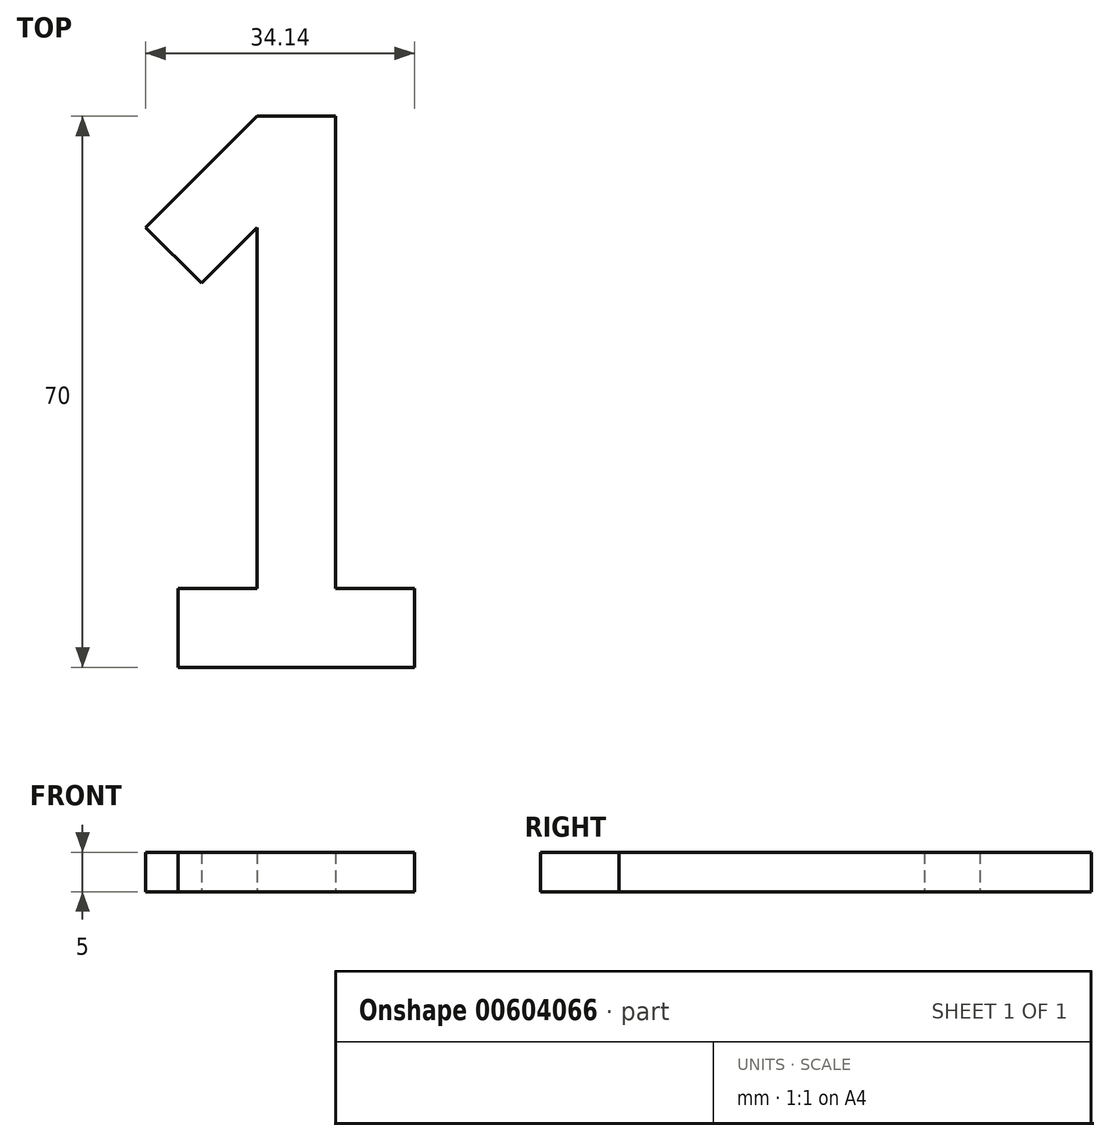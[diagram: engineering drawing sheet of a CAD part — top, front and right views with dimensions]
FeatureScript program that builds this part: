
annotation { "Feature Type Name" : "Feature", "Feature Type Description" : "" }
export const myFeature = defineFeature(function(context is Context, id is Id, definition is map)
    precondition{}
    {
        {
            var Q0;
            Q0=qCreatedBy(makeId("Top.planeOp"),FACE);
            var sketch = newSketch(context, id + "F0", { "sketchPlane" : qUnion([Q0])});
            skLineSegment(sketch, "E0.bottom", {"start": v(-3.56, 0) * mm, "end": v(6.44, 0) * mm});
            skLineSegment(sketch, "E0.top", {"start": v(-3.56, 70) * mm, "end": v(6.44, 70) * mm});
            skLineSegment(sketch, "E0.left", {"start": v(-3.56, 10) * mm, "end": v(-3.56, 55.86) * mm});
            skLineSegment(sketch, "E0.right", {"start": v(6.44, 10) * mm, "end": v(6.44, 70) * mm});
            skLineSegment(sketch, "E1.bottom", {"start": v(-13.56, 10) * mm, "end": v(-3.56, 10) * mm});
            skLineSegment(sketch, "E1.top", {"start": v(-13.56, 0) * mm, "end": v(16.44, 0) * mm});
            skLineSegment(sketch, "E1.left", {"start": v(-13.56, 10) * mm, "end": v(-13.56, 0) * mm});
            skLineSegment(sketch, "E1.right", {"start": v(16.44, 10) * mm, "end": v(16.44, 0) * mm});
            skLineSegment(sketch, "E2.trimOffspring", {"start": v(6.44, 10) * mm, "end": v(16.44, 10) * mm});
            skLineSegment(sketch, "E3", {"start": v(-3.56, 70) * mm, "end": v(-17.7, 55.86) * mm});
            skLineSegment(sketch, "E4", {"start": v(-17.7, 55.86) * mm, "end": v(-10.63, 48.79) * mm});
            skLineSegment(sketch, "E5", {"start": v(-10.63, 48.79) * mm, "end": v(-3.56, 55.86) * mm});
            skSolve(sketch);
        }
        {
            var Q0;
            Q0 = qSketchRegion(id + "F0", true);
            extrude(context, id + "F1", {"entities" : qUnion([Q0]), "depth" : 5 * mm, "offsetDistance" : 25.4 * mm});
        }
    });
